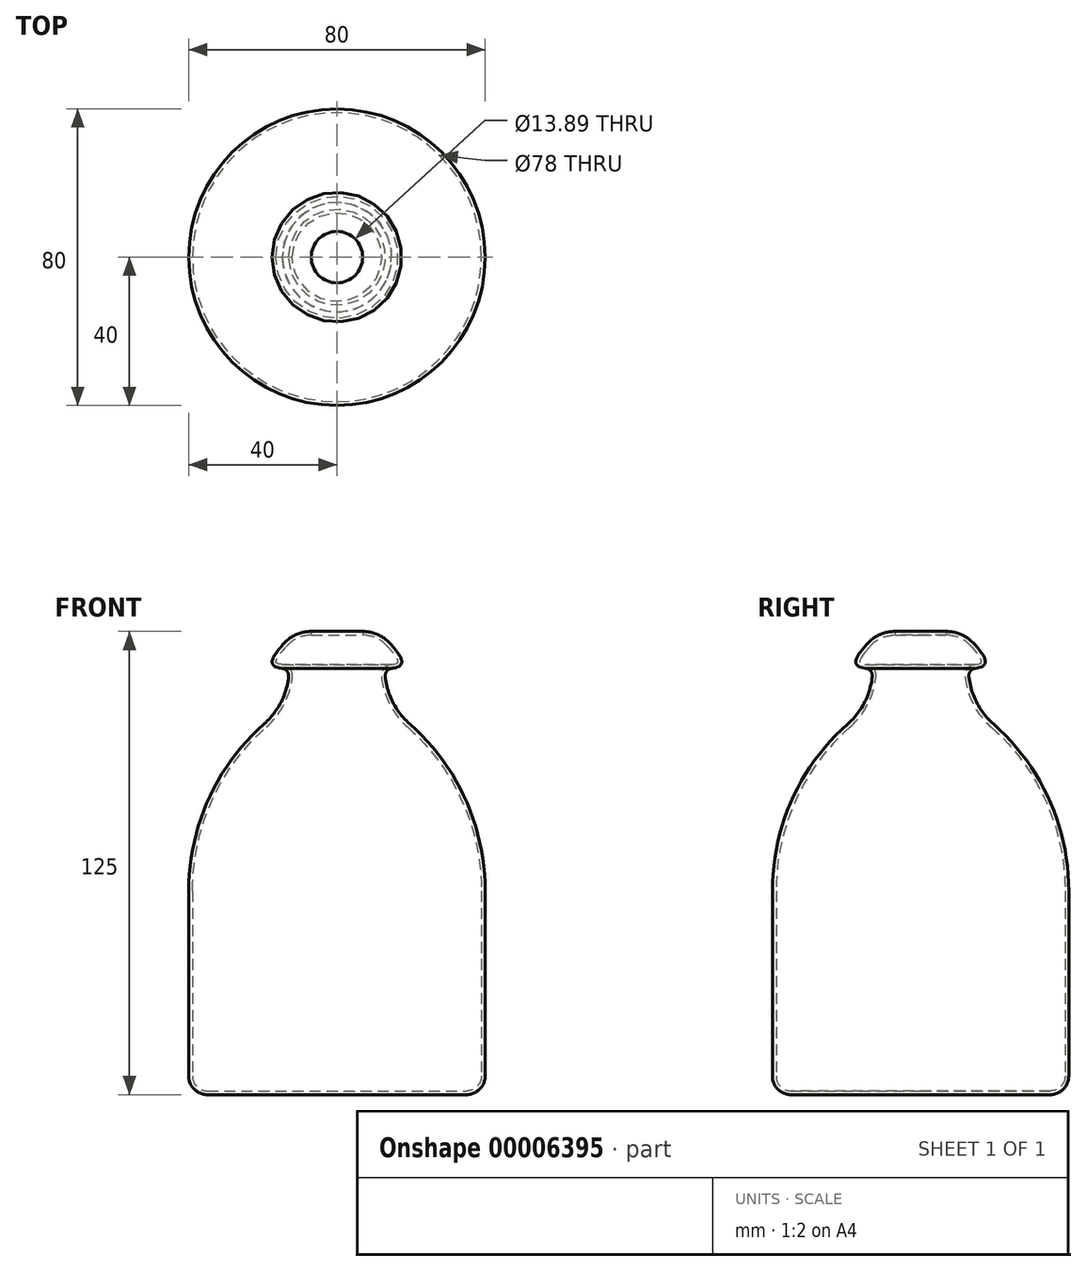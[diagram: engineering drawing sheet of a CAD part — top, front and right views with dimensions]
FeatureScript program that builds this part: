
annotation { "Feature Type Name" : "Feature", "Feature Type Description" : "" }
export const myFeature = defineFeature(function(context is Context, id is Id, definition is map)
    precondition{}
    {
        {
            var Q0;
            Q0=qCreatedBy(makeId("Front.planeOp"),FACE);
            var sketch = newSketch(context, id + "F0", { "sketchPlane" : qUnion([Q0])});
            skLineSegment(sketch, "E0", {"start": v(0, -24.35) * mm, "end": v(0, 0) * mm, "construction": true});
            skLineSegment(sketch, "E1", {"start": v(0, 0) * mm, "end": v(40, 0) * mm});
            skLineSegment(sketch, "E2", {"start": v(40, 0) * mm, "end": v(40, 55) * mm});
            skArc(sketch, "E3", {"start": v(40, 55) * mm, "mid": v(34.69, 79.69) * mm, "end": v(19.69, 100) * mm});
            skArc(sketch, "E4", {"start": v(12.92, 115) * mm, "mid": v(14.69, 106.77) * mm, "end": v(19.69, 100) * mm});
            skLineSegment(sketch, "E5", {"start": v(12.92, 115) * mm, "end": v(12.92, 130.1) * mm, "construction": true});
            skLineSegment(sketch, "E6", {"start": v(0, 0) * mm, "end": v(0, 125) * mm});
            skLineSegment(sketch, "E7", {"start": v(0, 125) * mm, "end": v(6.95, 125) * mm});
            skLineSegment(sketch, "E8", {"start": v(12.92, 115) * mm, "end": v(20, 115) * mm});
            skLineSegment(sketch, "E9", {"start": v(20, 115) * mm, "end": v(14.6, 121.43) * mm});
            skArc(sketch, "E10", {"start": v(6.95, 125) * mm, "mid": v(11.17, 124.06) * mm, "end": v(14.6, 121.43) * mm});
            skSolve(sketch);
        }
        {
            var Q0;
            Q0=makeQuery(id+"F0.imprint","IMPRINT",FACE,{"disambiguationData":[TD([[makeQuery(id+"F0.imprint","IMPRINT",EDGE,{"derivedFrom":sQuery(id+"F0.wireOp",EDGE,"E1")}),1.0]])]});
            var Q1;
            Q1=sQuery(id+"F0.wireOp",EDGE,"E0");
            revolve(context, id + "F1", {"entities" : qUnion([Q0]), "axis" : qUnion([Q1]), "revolveType" : RevolveType.FULL});
        }
        {
            var Q0;
            Q0=makeQuery(id+"F1.opRevolve","SWEPT_EDGE",EDGE,{"disambiguationData":[OSD([sQuery(id+"F0.wireOp",EDGE,"E8"),sQuery(id+"F0.wireOp",EDGE,"E9")])]});
            fillet(context, id + "F2", {"entities" : qUnion([Q0]), "radius" : 3 * mm, "tangentPropagation" : true, "rho" : 0.5, "crossSection" : FilletCrossSection.CONIC, "allowEdgeOverflow" : false});
        }
        {
            var Q0;
            Q0=makeQuery(id+"F1.opRevolve","SWEPT_EDGE",EDGE,{"disambiguationData":[OSD([sQuery(id+"F0.wireOp",EDGE,"E4"),sQuery(id+"F0.wireOp",EDGE,"E8")])]});
            fillet(context, id + "F3", {"entities" : qUnion([Q0]), "radius" : 2 * mm, "tangentPropagation" : true, "allowEdgeOverflow" : false});
        }
        {
            var Q0;
            Q0=makeQuery(id+"F1.opRevolve","SWEPT_EDGE",EDGE,{"disambiguationData":[OSD([sQuery(id+"F0.wireOp",EDGE,"E1"),sQuery(id+"F0.wireOp",EDGE,"E2")])]});
            fillet(context, id + "F4", {"entities" : qUnion([Q0]), "radius" : 5 * mm, "tangentPropagation" : true, "allowEdgeOverflow" : false});
        }
        {
            var Q0;
            Q0=makeQuery(id+"F1.opRevolve","SWEPT_FACE",FACE,{"disambiguationData":[OSD([sQuery(id+"F0.wireOp",EDGE,"E7")])]});
            shell(context, id + "F5", {"entities" : qUnion([Q0]), "thickness" : 1 * mm});
        }
    });
